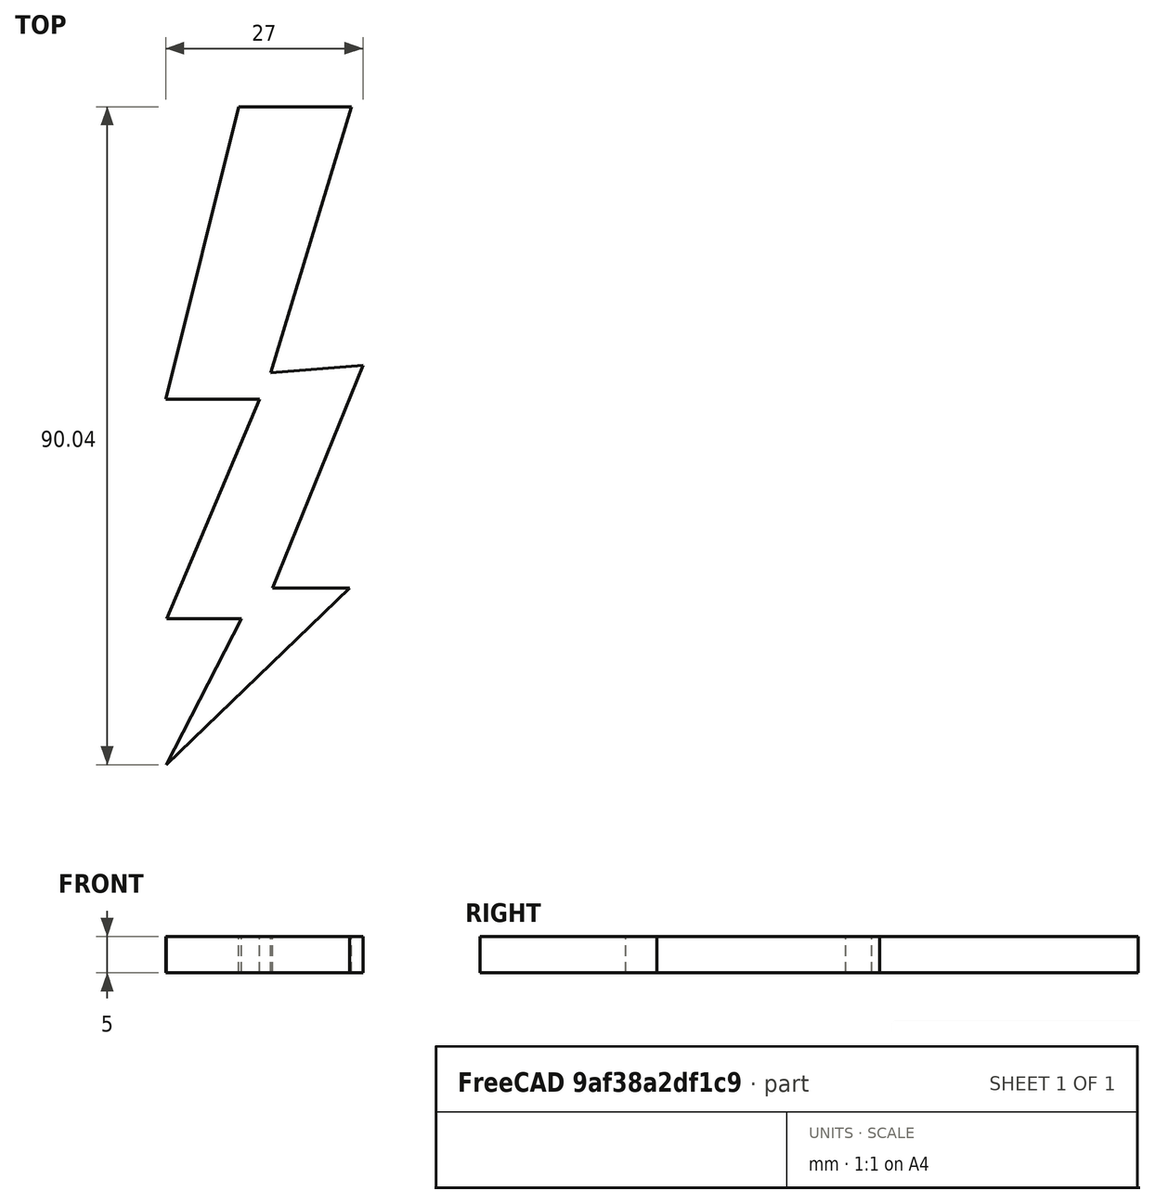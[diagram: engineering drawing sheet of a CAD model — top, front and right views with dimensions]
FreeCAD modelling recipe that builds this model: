
FCSTD DOCUMENT  (FreeCAD 1.0R39319 (Git))
Label: ojt1_t16r03_ray
License: All rights reserved
LicenseURL: https://en.wikipedia.org/wiki/All_rights_reserved
objects: Sketcher::SketchObject×1, PartDesign::Pad×1, PartDesign::Body×1
note: 6 computed .brp shape members not serialized (recipe doc carries the construction recipe); baked Part::Feature solids carry a one-line shape summary decoded from their .brp

FEATURE [Sketcher::SketchObject] Sketch
  ArcFitTolerance = 1e-06
  AttachmentSupport = -> [XY_Plane]
  FullyConstrained = false
  MakeInternals = false
  MapMode = 5
  sketch-geometry (11):
    g0: LineSegment StartX=9.94334 StartY=9.96124 StartZ=0 EndX=22.7763 EndY=9.96124 EndZ=0
    g1: LineSegment StartX=22.7763 StartY=9.96124 StartZ=0 EndX=10.0784 EndY=-20.1192 EndZ=0
    g2: LineSegment StartX=10.0784 StartY=-20.1192 StartZ=0 EndX=20.2909 EndY=-20.1192 EndZ=0
    g3: LineSegment StartX=20.2909 StartY=-20.1192 StartZ=0 EndX=10.0259 EndY=-40.0748 EndZ=0
    g4: LineSegment StartX=10.0259 StartY=-40.0748 StartZ=0 EndX=35.1351 EndY=-15.8802 EndZ=0
    g5: LineSegment StartX=35.1351 StartY=-15.8802 StartZ=0 EndX=24.5479 EndY=-15.8802 EndZ=0
    g6: LineSegment StartX=24.5479 StartY=-15.8802 StartZ=0 EndX=36.9427 EndY=14.5903 EndZ=0
    g7: LineSegment StartX=36.9427 StartY=14.5903 StartZ=0 EndX=24.2897 EndY=13.5574 EndZ=0
    g8: LineSegment StartX=24.2897 StartY=13.5574 StartZ=0 EndX=35.3934 EndY=49.9671 EndZ=0
    g9: LineSegment StartX=35.3934 StartY=49.9671 StartZ=0 EndX=19.8999 EndY=49.9671 EndZ=0
    g10: LineSegment StartX=19.8999 StartY=49.9671 StartZ=0 EndX=9.94334 EndY=9.96124 EndZ=0
  constraints (15):
    c: Horizontal(g0)
    c: Coincident(g0,g1)
    c: Coincident(g1,g2)
    c: Horizontal(g2)
    c: Coincident(g2,g3)
    c: Coincident(g3,g4)
    c: Coincident(g4,g5)
    c: Horizontal(g5)
    c: Coincident(g5,g6)
    c: Coincident(g6,g7)
    c: Coincident(g7,g8)
    c: Coincident(g8,g9)
    c: Horizontal(g9)
    c: Coincident(g9,g10)
    c: Coincident(g10,g0)
FEATURE [PartDesign::Pad] Pad
  Direction = (0,0,1)
  Length = 5
  Length2 = 10
  Profile = -> Sketch
  ReferenceAxis = -> Sketch [N_Axis]
  Refine = true
  Suppressed = false
  Type = 0
FEATURE [PartDesign::Body] Body
  AllowCompound = false
  Group = -> [Sketch,Pad]
  Origin = -> Origin
  Tip = -> Pad
